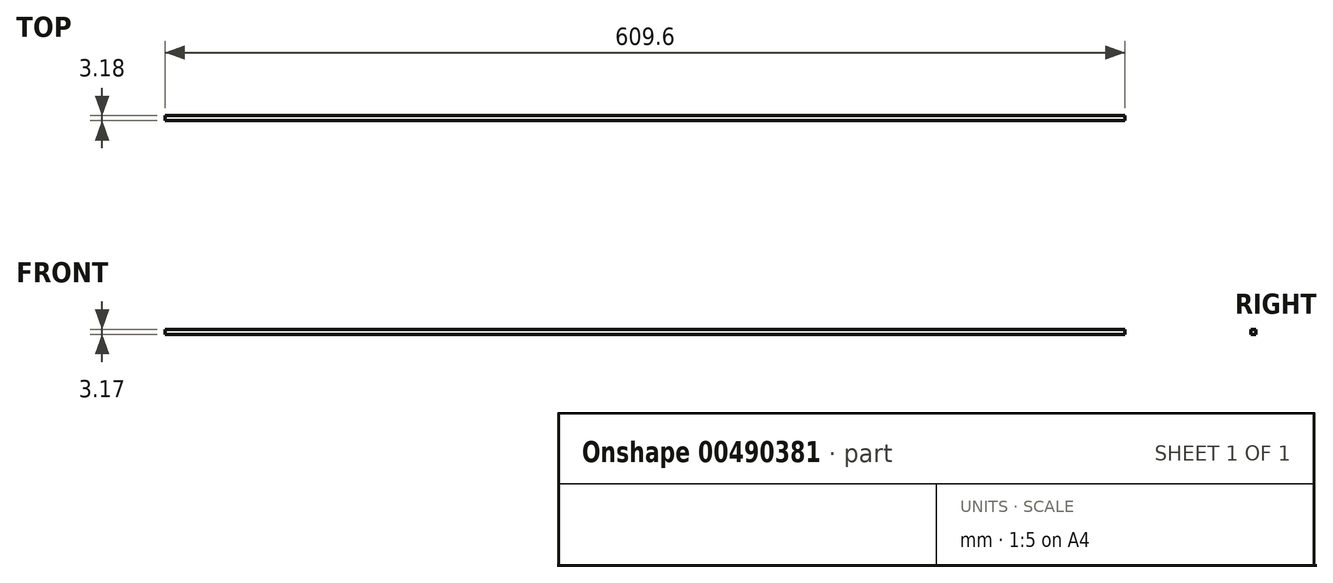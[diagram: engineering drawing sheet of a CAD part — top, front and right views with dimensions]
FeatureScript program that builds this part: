
annotation { "Feature Type Name" : "Feature", "Feature Type Description" : "" }
export const myFeature = defineFeature(function(context is Context, id is Id, definition is map)
    precondition{}
    {
        {
            var Q0;
            Q0=qCreatedBy(makeId("Right.planeOp"),FACE);
            var sketch = newSketch(context, id + "F0", { "sketchPlane" : qUnion([Q0])});
            skLineSegment(sketch, "E0.bottom", {"start": v(43, 41.07) * mm, "end": v(39.82, 41.07) * mm});
            skLineSegment(sketch, "E0.top", {"start": v(43, 37.9) * mm, "end": v(39.82, 37.9) * mm});
            skLineSegment(sketch, "E0.left", {"start": v(43, 41.07) * mm, "end": v(43, 37.9) * mm});
            skLineSegment(sketch, "E0.right", {"start": v(39.82, 41.07) * mm, "end": v(39.82, 37.9) * mm});
            skSolve(sketch);
        }
        {
            var Q0;
            Q0=makeQuery(id+"F0.imprint","IMPRINT",FACE,{"disambiguationData":[TD([[makeQuery(id+"F0.imprint","IMPRINT",EDGE,{"derivedFrom":sQuery(id+"F0.wireOp",EDGE,"E0.bottom")}),1.0]])]});
            extrude(context, id + "F1", {"entities" : qUnion([Q0]), "depth" : 609.6 * mm});
        }
    });
